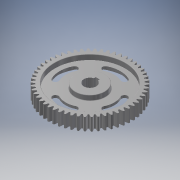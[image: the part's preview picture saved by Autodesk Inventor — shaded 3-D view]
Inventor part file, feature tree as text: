
AUTODESK INVENTOR PART (.ipt)
format: ipt  version: 2018 (Build 220112000, 112)  size: 536,064 bytes
history: native  units: mm (DEFAULTED — no unit token found)
features: sketch x6, extrude x5, plane x4, other x3, fillet x3, mirror x2, projected_geometry x2, pattern_circular x1
ambient origin geometry x8: Origin, YZ Plane, XZ Plane, XY Plane, X Axis, Y Axis, Z Axis, Center Point
bodies: Body1 (feature_tree), Body2 (feature_tree)
feature tree (26):
  extrude  "Extrusion1"  Depth=25.0mm TaperAngle=0.0deg
  plane  "Work Plane2"
  plane  "Work Plane8"
  plane  "Work Plane9"
  other  "Engranaje recto"
  extrude  "Extrusión2"  Depth=10.0mm TaperAngle=0.0deg
  extrude  "Extrusión3"  Depth=0.581776mm TaperAngle=0.0deg
  extrude  "Extrusión5"  TaperAngle=0.0deg  [1 undecoded]
  extrude  "Extrusión6"  Depth=108.0mm
  pattern_circular  "Patrón circular1"  Count=14  [1 undecoded]
  fillet  "Empalme1"  Radius=60.0mm
  fillet  "Empalme2"  Radius=10.0mm
  fillet  "Empalme3"  Radius=25.0mm
  plane  "Work Plane11"
  mirror  "Mirror1"
  mirror  "Mirror2"
  sketch  "Sketch1"  dims[d0=168.0mm d1=25.0mm d2=0.0mm]
  sketch  "Sketch2"  dims[d3=162.0mm d4=10.0mm d5=0.0mm]
  other  "Srf1"
  sketch  "Boceto3"  dims[d16=108.0mm d17=0.0mm d34=0.581776mm]
  sketch  "Boceto4"  dims[d39=0.0mm d41=0.0mm]
  sketch  "Boceto6"  dims[d43=108.0mm d46=108.0mm]
  projected_geometry  "Contorno proyectado2"
  sketch  "Boceto7"  dims[d47=0.0mm d48=0.0mm d49=140.0mm d50=60.0mm d51=10.0mm d52=0.0mm d53=25.0mm d54=10.0mm d55=0.0mm d60=8.0mm d61=6.0mm d62=10.0mm d63=0.0mm d64=50.0mm d65=12.0mm d66=10.0mm d67=0.0mm d68=40.0mm d69=360.0deg d71=1.0mm d72=1.0mm d73=1.0mm]
  projected_geometry  "Contorno proyectado3"
  other  "Diámetro de separación"
note: 2 required parameter values undecoded (feature->parameter linkage not recoverable at this tier; creation-order binding heuristic only, values carry confidence <= 0.55)
